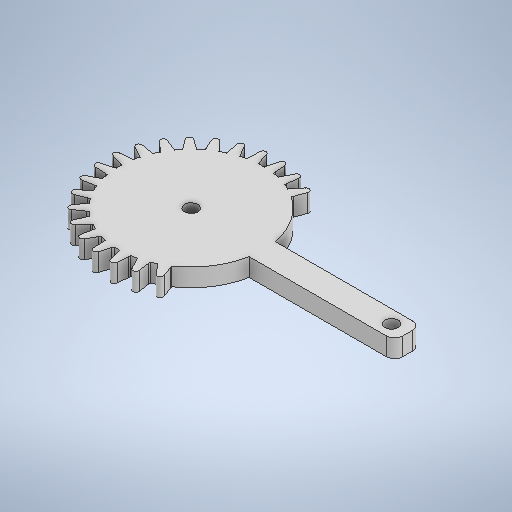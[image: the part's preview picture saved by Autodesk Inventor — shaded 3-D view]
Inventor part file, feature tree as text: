
AUTODESK INVENTOR PART (.ipt)
format: ipt  version: 2025.1 (Build 291241020, 241B)  size: 760,320 bytes
history: native  units: in
note: dims shown in document units (in); Inventor stores cm internally (conversion verified against a paired STEP export)
features: extrude x14, sketch x14, other x3, fillet x2, pattern_circular x1
ambient origin geometry x8: Origin, YZ Plane, XZ Plane, XY Plane, X Axis, Y Axis, Z Axis, Center Point
bodies: Solid1 (feature_tree)
feature tree (34):
  other  "servoMoldAssembly.iam"
  other  "block.ipt:1"
  other  "sg90horn.ipt:1"
  extrude  "Extrusion1"  Depth=0.3937in TaperAngle=0.0deg
  extrude  "Extrusion2"  Depth=0.3937in TaperAngle=0.0deg
  extrude  "Extrusion3"  Depth=0.0591in TaperAngle=0.0deg
  extrude  "Extrusion4"  Depth=0.0591in TaperAngle=0.0deg
  extrude  "Extrusion5"  Depth=1.9685in
  extrude  "Extrusion6"  Depth=0.3937in TaperAngle=0.0deg
  extrude  "Extrusion7"  Depth=0.3937in TaperAngle=0.0deg
  extrude  "Extrusion8"  Depth=0.1299in
  extrude  "Extrusion10"  Depth=0.0787in TaperAngle=0.0deg
  extrude  "Extrusion11"  Depth=0.0787in TaperAngle=0.0deg
  fillet  "Fillet1"  Radius=0.0787in
  extrude  "Extrusion12"  Depth=0.8268in
  fillet  "Fillet2"  Radius=1.1934in
  extrude  "Extrusion13"  TaperAngle=90.0deg  [1 undecoded]
  pattern_circular  "Circular Pattern2"  Count=20 Angle=240.0deg
  extrude  "Extrusion14"  Depth=0.3937in
  extrude  "Extrusion15"  Depth=0.3937in TaperAngle=0.0deg
  sketch  "Sketch3"  dims[d0=0.3937in d1=0.3937in d2=0.0in]
  sketch  "Sketch4"  dims[d3=0.2795in d4=0.3937in d5=0.0in]
  sketch  "Sketch5"  dims[d6=0.0591in d7=0.0in d8=0.0591in d9=0.0in]
  sketch  "Sketch6"  dims[d10=0.0591in d11=0.0in d12=0.0591in d13=0.0in]
  sketch  "Sketch7"  dims[d14=1.4173in d15=1.9685in]
  sketch  "Sketch8"  dims[d16=0.0in d17=0.3937in d18=0.0in]
  sketch  "Sketch9"  dims[d19=0.3937in d20=0.0in d29=0.2362in d30=0.0in]
  sketch  "Sketch10"  dims[d31=0.2362in d32=0.1299in]
  sketch  "Sketch12"  dims[d33=0.0787in d34=0.2362in d35=0.0in]
  sketch  "Sketch13"  dims[d36=0.0787in d37=0.2362in d38=0.0in d39=0.0787in]
  sketch  "Sketch14"  dims[d40=0.0984in d41=0.8268in d42=1.1934in]
  sketch  "Sketch15"  dims[d43=0.0591in d44=90.0deg]
  sketch  "Sketch16"  dims[d45=0.3937in d46=0.0in d47=7.874in d48=240.0deg]
  sketch  "Sketch17"  dims[d50=0.3937in d51=0.0in d52=0.1299in d53=0.3937in d54=0.0in]
note: 1 required parameter value undecoded (feature->parameter linkage not recoverable at this tier; creation-order binding heuristic only, values carry confidence <= 0.55)
